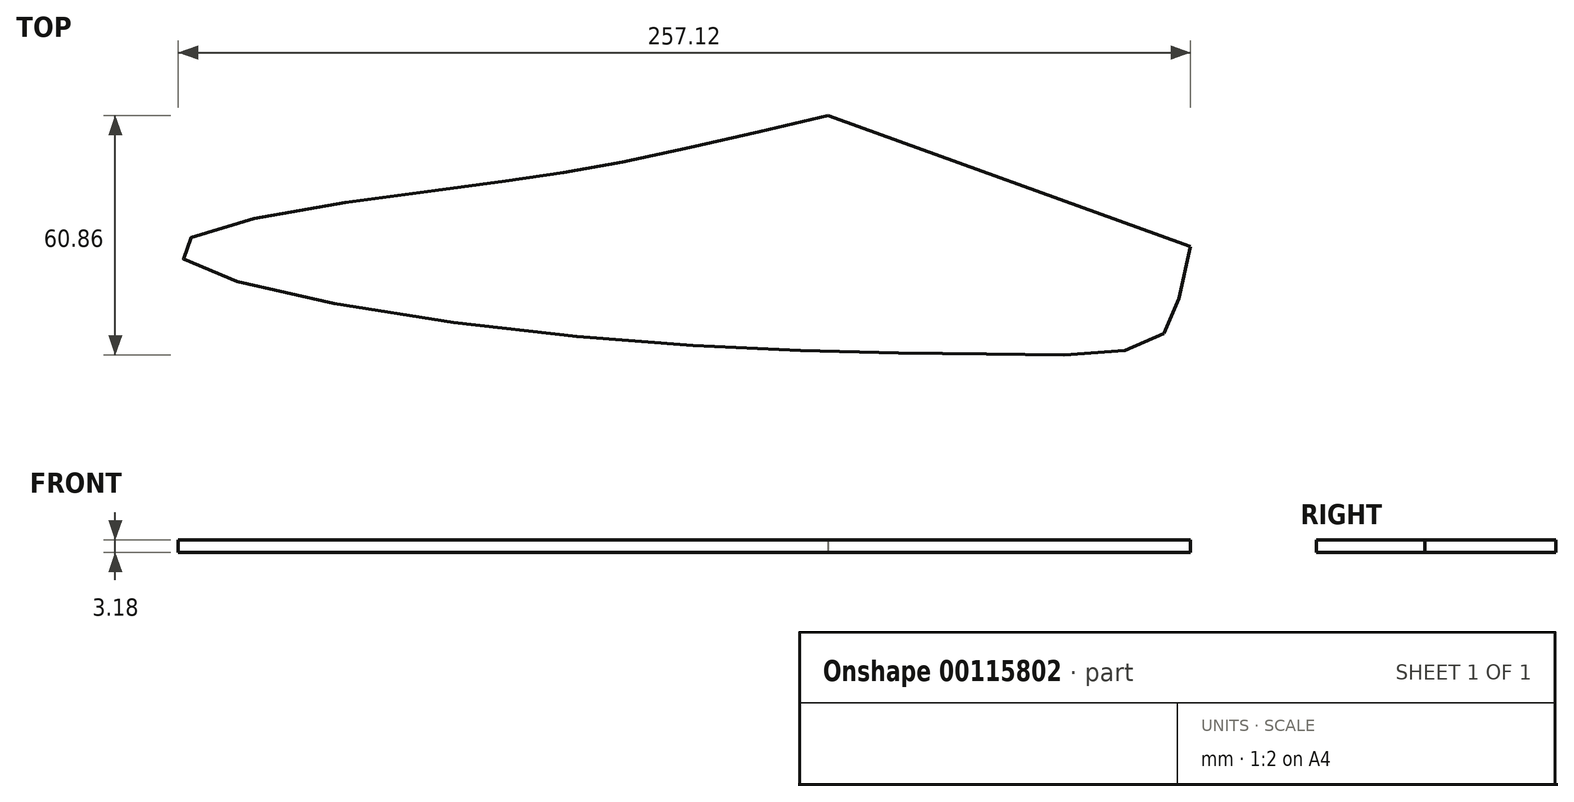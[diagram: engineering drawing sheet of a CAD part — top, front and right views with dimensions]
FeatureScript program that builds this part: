
annotation { "Feature Type Name" : "Feature", "Feature Type Description" : "" }
export const myFeature = defineFeature(function(context is Context, id is Id, definition is map)
    precondition{}
    {
        {
            var Q0;
            Q0=qCreatedBy(makeId("Top.planeOp"),FACE);
            var sketch = newSketch(context, id + "F0", { "sketchPlane" : qUnion([Q0])});
            skFitSpline(sketch, "E0", {"points": [v(-252.94, 43.7) * mm, v(-308.26, 31.25) * mm, v(-355.3, 24.33) * mm, v(-417.94, 9.81) * mm, v(-330.59, -11.05) * mm, v(-206.89, -17.03) * mm, v(-168.06, -12.2) * mm, v(-160.88, 10.4) * mm], "startDerivative": vector(-378.76, -89.89) * mm, "endDerivative": vector(99.15, 347.18) * mm});
            skLineSegment(sketch, "E1", {"start": v(-252.94, 43.7) * mm, "end": v(-160.88, 10.4) * mm});
            skSolve(sketch);
        }
        {
            var Q0;
            Q0=makeQuery(id+"F0.imprint","IMPRINT",FACE,{"disambiguationData":[TD([[makeQuery(id+"F0.imprint","IMPRINT",EDGE,{"derivedFrom":sQuery(id+"F0.wireOp",EDGE,"E0")}),1.0]])]});
            extrude(context, id + "F1", {"entities" : qUnion([Q0]), "depth" : 3.17 * mm});
        }
    });
